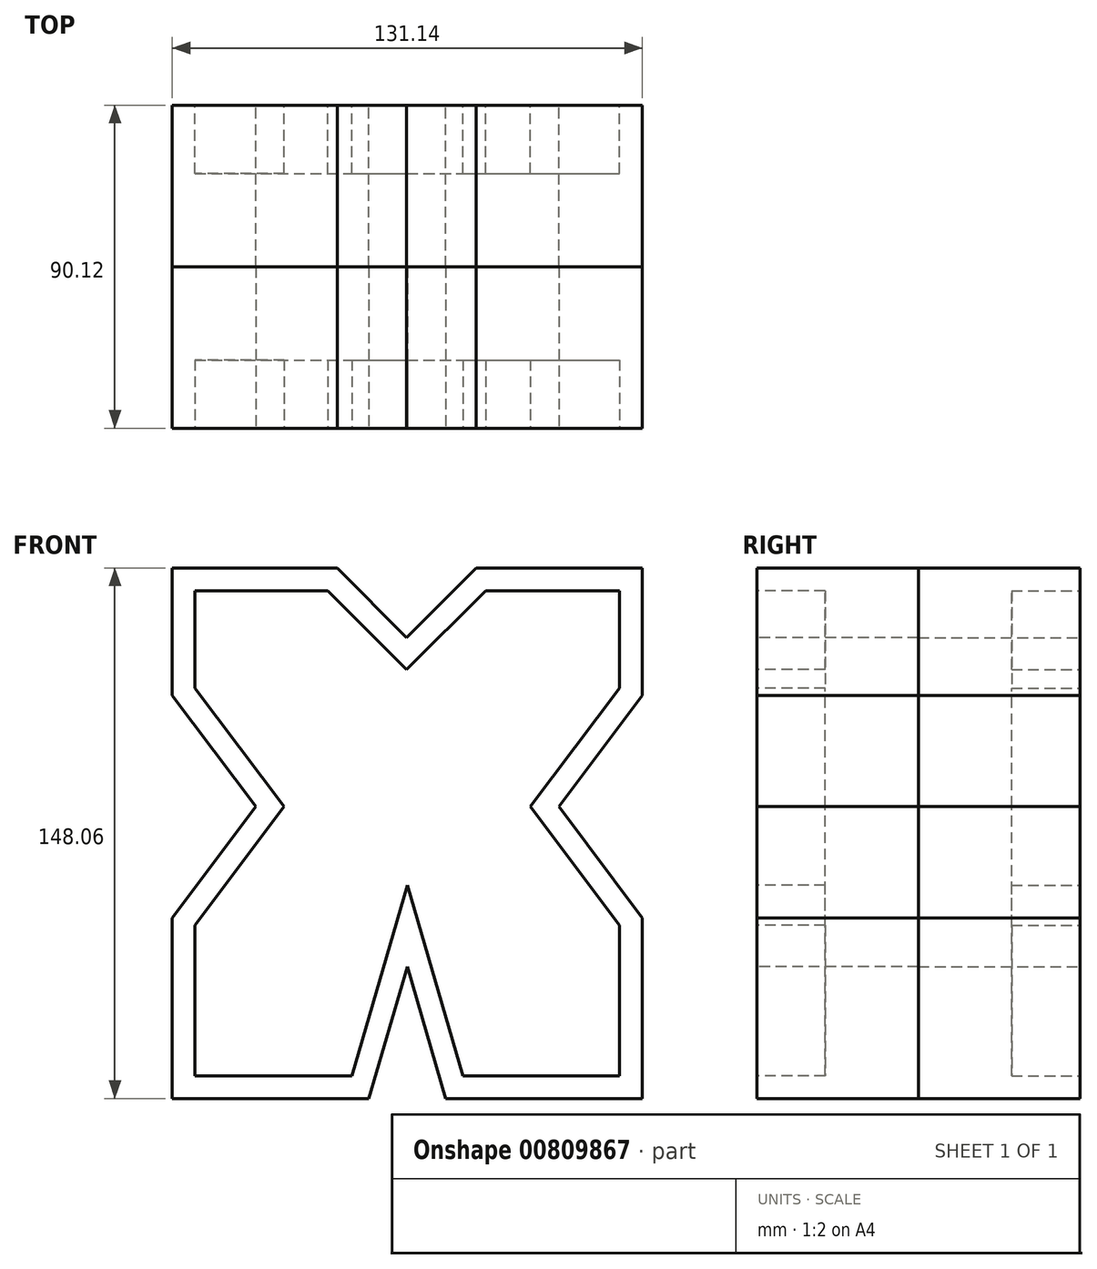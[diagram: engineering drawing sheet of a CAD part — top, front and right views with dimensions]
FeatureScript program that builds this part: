
annotation { "Feature Type Name" : "Feature", "Feature Type Description" : "" }
export const myFeature = defineFeature(function(context is Context, id is Id, definition is map)
    precondition{}
    {
        {
            var Q0;
            Q0=qCreatedBy(makeId("Front.planeOp"),FACE);
            var sketch = newSketch(context, id + "F0", { "sketchPlane" : qUnion([Q0])});
            skLineSegment(sketch, "E0", {"start": v(0, 0) * mm, "end": v(54.86, 0) * mm});
            skLineSegment(sketch, "E1", {"start": v(54.86, 0) * mm, "end": v(65.57, 36.8) * mm});
            skLineSegment(sketch, "E2", {"start": v(65.57, 36.8) * mm, "end": v(76.28, 0) * mm});
            skLineSegment(sketch, "E3", {"start": v(76.28, 0) * mm, "end": v(131.14, 0) * mm});
            skLineSegment(sketch, "E4", {"start": v(131.14, 0) * mm, "end": v(131.14, 50.42) * mm});
            skLineSegment(sketch, "E5", {"start": v(131.14, 50.42) * mm, "end": v(107.85, 81.43) * mm});
            skLineSegment(sketch, "E6", {"start": v(107.85, 81.43) * mm, "end": v(131.14, 112.45) * mm});
            skLineSegment(sketch, "E7", {"start": v(131.14, 112.45) * mm, "end": v(131.14, 148.06) * mm});
            skLineSegment(sketch, "E8", {"start": v(131.14, 148.06) * mm, "end": v(84.79, 148.06) * mm});
            skLineSegment(sketch, "E9", {"start": v(84.79, 148.06) * mm, "end": v(65.4, 128.66) * mm});
            skLineSegment(sketch, "E10", {"start": v(65.4, 128.66) * mm, "end": v(46, 148.06) * mm});
            skLineSegment(sketch, "E11", {"start": v(46, 148.06) * mm, "end": v(0, 148.06) * mm});
            skLineSegment(sketch, "E12", {"start": v(0, 148.06) * mm, "end": v(0, 112.45) * mm});
            skLineSegment(sketch, "E13", {"start": v(0, 112.45) * mm, "end": v(23.3, 81.43) * mm});
            skLineSegment(sketch, "E14", {"start": v(23.3, 81.43) * mm, "end": v(0, 50.42) * mm});
            skLineSegment(sketch, "E15", {"start": v(0, 50.42) * mm, "end": v(0, 0) * mm});
            skLineSegment(sketch, "E16", {"start": v(6.35, 141.7) * mm, "end": v(43.37, 141.7) * mm});
            skLineSegment(sketch, "E17", {"start": v(43.37, 141.7) * mm, "end": v(65.4, 119.68) * mm});
            skLineSegment(sketch, "E18", {"start": v(65.4, 119.68) * mm, "end": v(87.42, 141.7) * mm});
            skLineSegment(sketch, "E19", {"start": v(87.42, 141.7) * mm, "end": v(124.8, 141.7) * mm});
            skLineSegment(sketch, "E20", {"start": v(124.8, 141.7) * mm, "end": v(124.8, 114.56) * mm});
            skLineSegment(sketch, "E21", {"start": v(124.8, 114.56) * mm, "end": v(99.9, 81.43) * mm});
            skLineSegment(sketch, "E22", {"start": v(99.9, 81.43) * mm, "end": v(124.8, 48.3) * mm});
            skLineSegment(sketch, "E23", {"start": v(6.35, 48.3) * mm, "end": v(31.23, 81.43) * mm});
            skLineSegment(sketch, "E24", {"start": v(31.23, 81.43) * mm, "end": v(6.35, 114.56) * mm});
            skLineSegment(sketch, "E25", {"start": v(6.35, 114.56) * mm, "end": v(6.35, 141.7) * mm});
            skLineSegment(sketch, "E26", {"start": v(6.35, 48.3) * mm, "end": v(6.35, 6.35) * mm});
            skLineSegment(sketch, "E27", {"start": v(6.35, 6.35) * mm, "end": v(50.1, 6.35) * mm});
            skLineSegment(sketch, "E28", {"start": v(50.1, 6.35) * mm, "end": v(65.57, 59.54) * mm});
            skLineSegment(sketch, "E29", {"start": v(65.57, 59.54) * mm, "end": v(81.04, 6.35) * mm});
            skLineSegment(sketch, "E30", {"start": v(81.04, 6.35) * mm, "end": v(124.8, 6.35) * mm});
            skLineSegment(sketch, "E31", {"start": v(124.8, 6.35) * mm, "end": v(124.8, 48.3) * mm});
            skSolve(sketch);
        }
        {
            var Q0;
            Q0=makeQuery(id+"F0.imprint","IMPRINT",FACE,{"disambiguationData":[TD([[makeQuery(id+"F0.imprint","IMPRINT",EDGE,{"derivedFrom":sQuery(id+"F0.wireOp",EDGE,"E0")}),1.0]])]});
            var Q1;
            Q1=makeQuery(id+"F0.imprint","IMPRINT",FACE,{"disambiguationData":[TD([[makeQuery(id+"F0.imprint","IMPRINT",EDGE,{"derivedFrom":sQuery(id+"F0.wireOp",EDGE,"E16")}),-1.0]])]});
            extrude(context, id + "F1", {"entities" : qUnion([Q0, Q1]), "oppositeDirection" : true, "depth" : 45.06 * mm, "offsetDistance" : 25.4 * mm});
        }
        {
            var Q0;
            Q0=makeQuery(id+"F0.imprint","IMPRINT",FACE,{"disambiguationData":[TD([[makeQuery(id+"F0.imprint","IMPRINT",EDGE,{"derivedFrom":sQuery(id+"F0.wireOp",EDGE,"E16")}),-1.0]])]});
            extrude(context, id + "F2", {"entities" : qUnion([Q0]), "operationType" : NewBodyOperationType.REMOVE, "endBound" : BoundingType.SYMMETRIC, "oppositeDirection" : true, "depth" : 38.1 * mm, "offsetDistance" : 25.4 * mm});
        }
        {
            var Q0;
            Q0=makeQuery(id+"F1.opExtrude","SWEPT_BODY",BODY,{"disambiguationData":[OSD([sQuery(id+"F0.wireOp",EDGE,"E0"),sQuery(id+"F0.wireOp",EDGE,"E1"),sQuery(id+"F0.wireOp",EDGE,"E2"),sQuery(id+"F0.wireOp",EDGE,"E3"),sQuery(id+"F0.wireOp",EDGE,"E4"),sQuery(id+"F0.wireOp",EDGE,"E5"),sQuery(id+"F0.wireOp",EDGE,"E6"),sQuery(id+"F0.wireOp",EDGE,"E7"),sQuery(id+"F0.wireOp",EDGE,"E8"),sQuery(id+"F0.wireOp",EDGE,"E9"),sQuery(id+"F0.wireOp",EDGE,"E10"),sQuery(id+"F0.wireOp",EDGE,"E11"),sQuery(id+"F0.wireOp",EDGE,"E12"),sQuery(id+"F0.wireOp",EDGE,"E13"),sQuery(id+"F0.wireOp",EDGE,"E14"),sQuery(id+"F0.wireOp",EDGE,"E15")])]});
            var Q1;
            Q1=makeQuery(id+"F1.opExtrude","CAP_FACE",FACE,{"disambiguationData":[OSD([sQuery(id+"F0.wireOp",EDGE,"E0"),sQuery(id+"F0.wireOp",EDGE,"E1"),sQuery(id+"F0.wireOp",EDGE,"E2"),sQuery(id+"F0.wireOp",EDGE,"E3"),sQuery(id+"F0.wireOp",EDGE,"E4"),sQuery(id+"F0.wireOp",EDGE,"E5"),sQuery(id+"F0.wireOp",EDGE,"E6"),sQuery(id+"F0.wireOp",EDGE,"E7"),sQuery(id+"F0.wireOp",EDGE,"E8"),sQuery(id+"F0.wireOp",EDGE,"E9"),sQuery(id+"F0.wireOp",EDGE,"E10"),sQuery(id+"F0.wireOp",EDGE,"E11"),sQuery(id+"F0.wireOp",EDGE,"E12"),sQuery(id+"F0.wireOp",EDGE,"E13"),sQuery(id+"F0.wireOp",EDGE,"E14"),sQuery(id+"F0.wireOp",EDGE,"E15")])],"isStart":false});
            mirror(context, id + "F3", {"entities" : qUnion([Q0]), "mirrorPlane" : qUnion([Q1])});
        }
    });
